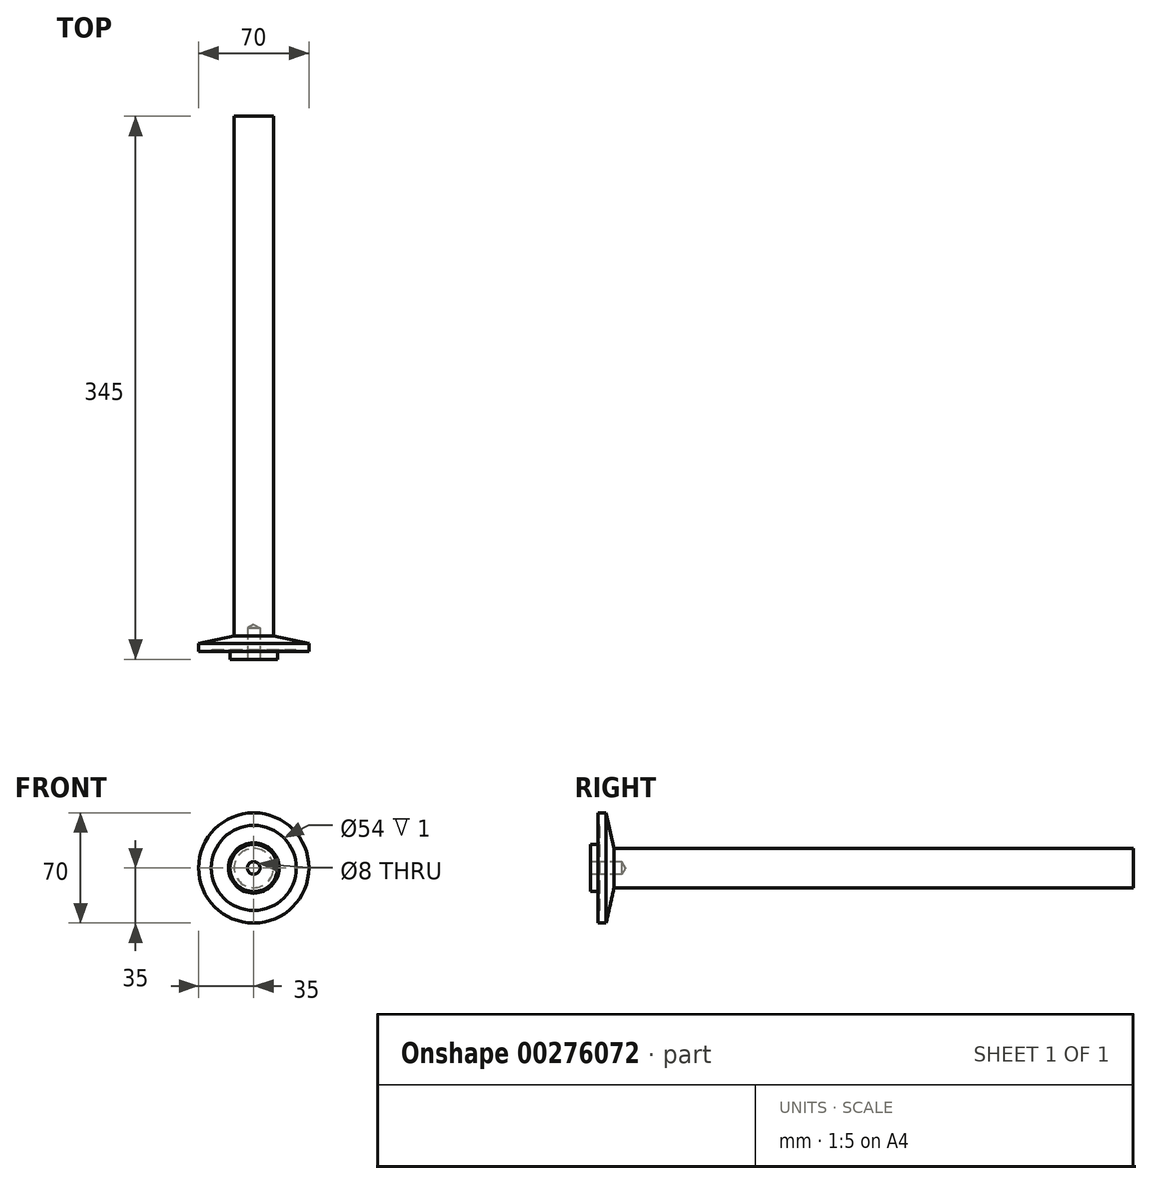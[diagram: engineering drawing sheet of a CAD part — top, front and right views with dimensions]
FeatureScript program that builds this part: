
annotation { "Feature Type Name" : "Feature", "Feature Type Description" : "" }
export const myFeature = defineFeature(function(context is Context, id is Id, definition is map)
    precondition{}
    {
        {
            var Q0;
            Q0=qCreatedBy(makeId("Top.planeOp"),FACE);
            var sketch = newSketch(context, id + "F0", { "sketchPlane" : qUnion([Q0])});
            skLineSegment(sketch, "E0.bottom", {"start": v(0, -165) * mm, "end": v(12.5, -165) * mm});
            skLineSegment(sketch, "E0.top", {"start": v(0, 165) * mm, "end": v(12.5, 165) * mm});
            skLineSegment(sketch, "E0.left", {"start": v(0, -165) * mm, "end": v(0, 165) * mm});
            skLineSegment(sketch, "E0.right", {"start": v(12.5, -165) * mm, "end": v(12.5, 165) * mm});
            skLineSegment(sketch, "E1.right", {"start": v(35, -170) * mm, "end": v(35, -175) * mm});
            skLineSegment(sketch, "E2", {"start": v(12.5, -165) * mm, "end": v(35, -170) * mm});
            skLineSegment(sketch, "E3", {"start": v(27, -175) * mm, "end": v(27, -174) * mm});
            skLineSegment(sketch, "E4", {"start": v(27, -174) * mm, "end": v(16, -174) * mm});
            skLineSegment(sketch, "E5", {"start": v(15, -175) * mm, "end": v(15, -180) * mm});
            skLineSegment(sketch, "E6", {"start": v(15, -180) * mm, "end": v(0, -180) * mm});
            skLineSegment(sketch, "E7", {"start": v(0, -165) * mm, "end": v(0, -180) * mm});
            skLineSegment(sketch, "E8", {"start": v(27, -175) * mm, "end": v(35, -175) * mm});
            skLineSegment(sketch, "E9", {"start": v(15, -175) * mm, "end": v(16, -175) * mm});
            skLineSegment(sketch, "E10", {"start": v(16, -175) * mm, "end": v(16, -174) * mm});
            skPoint(sketch, "E11.orphan", {"position": v(35, -165) * mm});
            skLineSegment(sketch, "E12", {"start": v(4, -180) * mm, "end": v(4, -160) * mm});
            skLineSegment(sketch, "E13", {"start": v(4, -160) * mm, "end": v(0, -157.7) * mm});
            skSolve(sketch);
        }
        {
            var Q0;
            {var subQ0=sQuery(id+"F0.wireOp",EDGE,"E2");Q0=makeQuery(id+"F0.imprint","IMPRINT",FACE,{"disambiguationData":[TD([[makeQuery(id+"F0.imprint","IMPRINT",EDGE,{"derivedFrom":subQ0}),-1.0]])]});}
            var Q1;
            Q1=makeQuery(id+"F0.imprint","IMPRINT",FACE,{"disambiguationData":[TD([[makeQuery(id+"F0.imprint","IMPRINT",EDGE,{"derivedFrom":sQuery(id+"F0.wireOp",EDGE,"E0.top")}),-1.0]])]});
            var Q2;
            Q2=sQuery(id+"F0.wireOp",EDGE,"E0.left");
            revolve(context, id + "F1", {"entities" : qUnion([Q0, Q1]), "axis" : qUnion([Q2]), "revolveType" : RevolveType.FULL});
        }
    });
